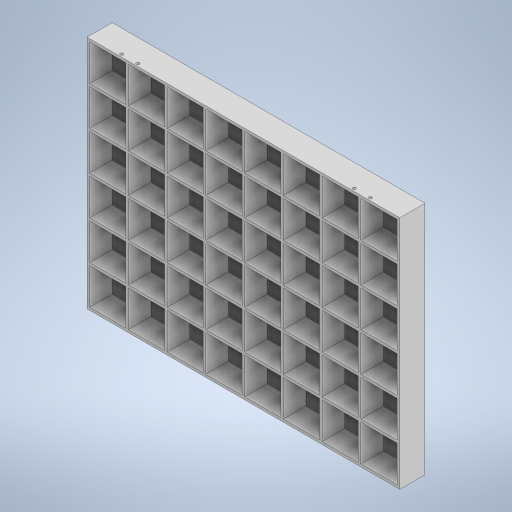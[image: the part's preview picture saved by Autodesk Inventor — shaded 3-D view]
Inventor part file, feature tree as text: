
AUTODESK INVENTOR PART (.ipt)
format: ipt  version: 2024 (Build 280153000, 153)  size: 548,864 bytes
history: native  units: in
note: dims shown in document units (in); Inventor stores cm internally (conversion verified against a paired STEP export)
features: extrude x3, sketch x3
ambient origin geometry x8: Origin, YZ Plane, XZ Plane, XY Plane, X Axis, Y Axis, Z Axis, Center Point
bodies: Solid1 (feature_tree)
feature tree (6):
  extrude  "Extrusion1"  Depth=10.2756in
  extrude  "Extrusion2"  TaperAngle=0.0deg  [1 undecoded]
  extrude  "Extrusion3"  Depth=0.1181in
  sketch  "Sketch1"  dims[d0=13.6614in d1=10.2756in]
  sketch  "Sketch2"  dims[d2=1.1024in d3=0.0in]
  sketch  "Sketch3"  dims[d4=1.5748in d5=0.1181in d6=0.1181in d7=1.5748in d8=3.1496in d10=1.6929in d11=2.3622in d13=1.6929in d16=0.9843in d17=0.0in d20=0.1181in d21=0.1299in d22=0.3543in d23=0.1299in d24=0.3543in d25=0.1299in d31=0.1299in d33=0.3937in d34=0.0in d35=0.7087in d36=1.3976in]
note: 1 required parameter value undecoded (feature->parameter linkage not recoverable at this tier; creation-order binding heuristic only, values carry confidence <= 0.55)
